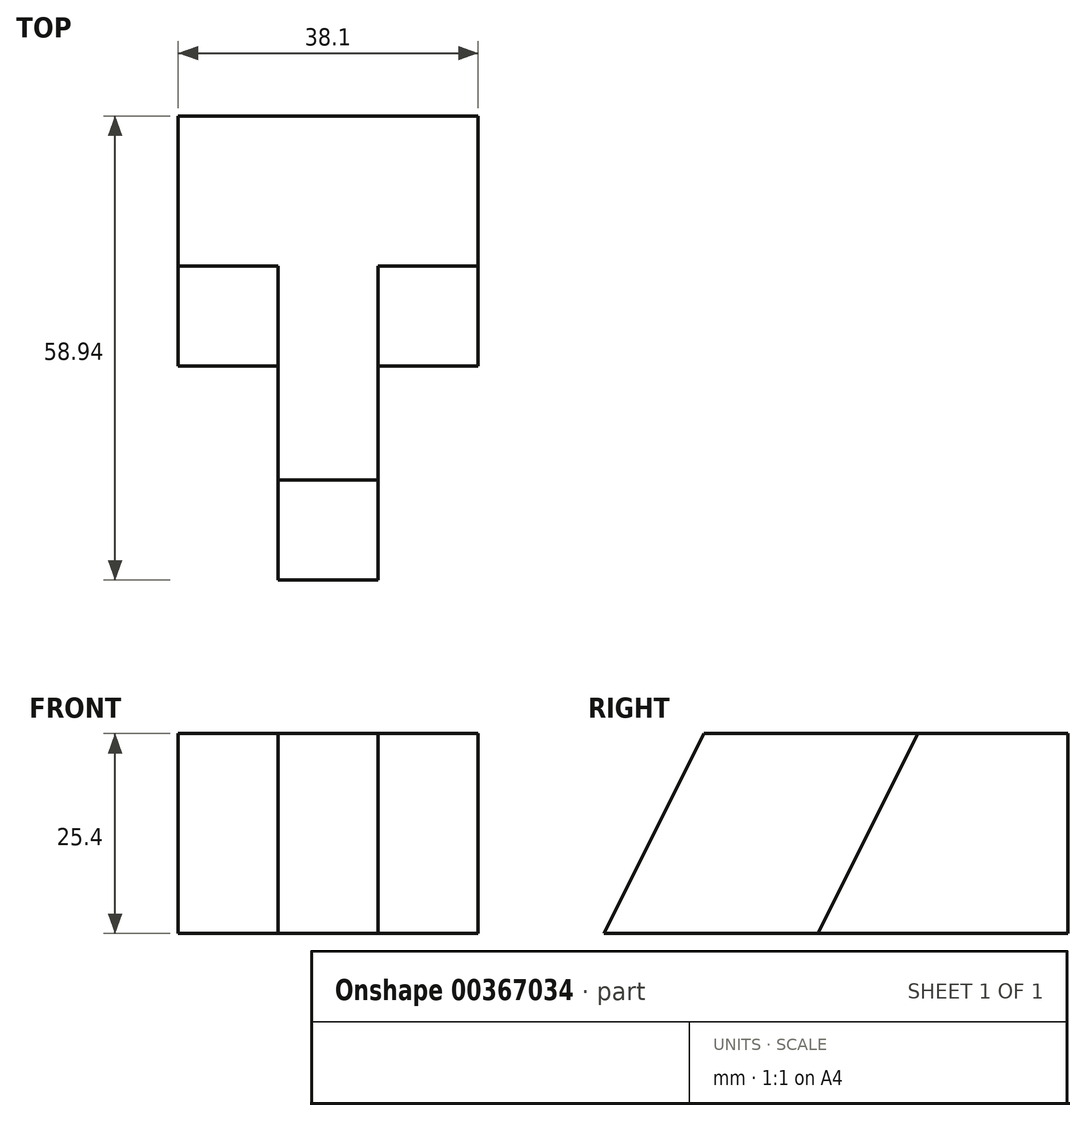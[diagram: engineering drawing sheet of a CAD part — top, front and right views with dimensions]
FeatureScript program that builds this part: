
annotation { "Feature Type Name" : "Feature", "Feature Type Description" : "" }
export const myFeature = defineFeature(function(context is Context, id is Id, definition is map)
    precondition{}
    {
        {
            var Q0;
            Q0=qCreatedBy(makeId("Top.planeOp"),FACE);
            var sketch = newSketch(context, id + "F0", { "sketchPlane" : qUnion([Q0])});
            skLineSegment(sketch, "E0", {"start": v(12.7, 0) * mm, "end": v(25.4, 0) * mm});
            skLineSegment(sketch, "E1", {"start": v(25.4, 0) * mm, "end": v(25.4, 27.2) * mm});
            skLineSegment(sketch, "E2", {"start": v(25.4, 27.2) * mm, "end": v(38.1, 27.2) * mm});
            skLineSegment(sketch, "E3", {"start": v(38.1, 27.2) * mm, "end": v(38.1, 58.94) * mm});
            skLineSegment(sketch, "E4", {"start": v(38.1, 58.94) * mm, "end": v(0, 58.94) * mm});
            skLineSegment(sketch, "E5", {"start": v(0, 58.94) * mm, "end": v(0, 27.2) * mm});
            skLineSegment(sketch, "E6", {"start": v(0, 27.2) * mm, "end": v(12.7, 27.2) * mm});
            skLineSegment(sketch, "E7", {"start": v(12.7, 27.2) * mm, "end": v(12.7, 0) * mm});
            skSolve(sketch);
        }
        {
            var Q0;
            Q0 = qSketchRegion(id + "F0", true);
            extrude(context, id + "F1", {"entities" : qUnion([Q0]), "depth" : 25.4 * mm});
        }
        {
            var Q0;
            Q0=makeQuery(id+"F1.opExtrude","SWEPT_FACE",FACE,{"disambiguationData":[OSD([sQuery(id+"F0.wireOp",EDGE,"E1")])]});
            var sketch = newSketch(context, id + "F2", { "sketchPlane" : qUnion([Q0])});
            skLineSegment(sketch, "E8", {"start": v(0, 0) * mm, "end": v(12.7, 25.4) * mm});
            skSolve(sketch);
        }
        {
            var Q0;
            Q0=makeQuery(id+"F1.opExtrude","SWEPT_FACE",FACE,{"disambiguationData":[OSD([sQuery(id+"F0.wireOp",EDGE,"E3")])]});
            var sketch = newSketch(context, id + "F3", { "sketchPlane" : qUnion([Q0])});
            skLineSegment(sketch, "E9", {"start": v(27.2, 0) * mm, "end": v(39.9, 25.4) * mm});
            skSolve(sketch);
        }
        {
            var Q0;
            Q0=makeQuery(id+"F1.opExtrude","SWEPT_FACE",FACE,{"disambiguationData":[OSD([sQuery(id+"F0.wireOp",EDGE,"E5")])]});
            var sketch = newSketch(context, id + "F4", { "sketchPlane" : qUnion([Q0])});
            skLineSegment(sketch, "E10", {"start": v(-39.9, 25.4) * mm, "end": v(-27.2, 0) * mm});
            skSolve(sketch);
        }
        {
            var Q0;
            {var subQ0=sQuery(id+"F3.wireOp",EDGE,"E9");Q0=makeQuery(id+"F3.imprint","IMPRINT",FACE,{"disambiguationData":[TD([[makeQuery(id+"F3.imprint","IMPRINT",EDGE,{"derivedFrom":subQ0}),1.0]])]});}
            extrude(context, id + "F5", {"entities" : qUnion([Q0]), "operationType" : NewBodyOperationType.REMOVE, "oppositeDirection" : true, "depth" : 12.7 * mm});
        }
        {
            var Q0;
            {var subQ0=sQuery(id+"F2.wireOp",EDGE,"E8");Q0=makeQuery(id+"F2.imprint","IMPRINT",FACE,{"disambiguationData":[TD([[makeQuery(id+"F2.imprint","IMPRINT",EDGE,{"derivedFrom":subQ0}),1.0]])]});}
            extrude(context, id + "F6", {"entities" : qUnion([Q0]), "operationType" : NewBodyOperationType.REMOVE, "oppositeDirection" : true, "depth" : 25.4 * mm});
        }
        {
            var Q0;
            {var subQ0=sQuery(id+"F4.wireOp",EDGE,"E10");Q0=makeQuery(id+"F4.imprint","IMPRINT",FACE,{"disambiguationData":[TD([[makeQuery(id+"F4.imprint","IMPRINT",EDGE,{"derivedFrom":subQ0}),1.0]])]});}
            extrude(context, id + "F7", {"entities" : qUnion([Q0]), "operationType" : NewBodyOperationType.REMOVE, "oppositeDirection" : true, "depth" : 12.7 * mm});
        }
    });
